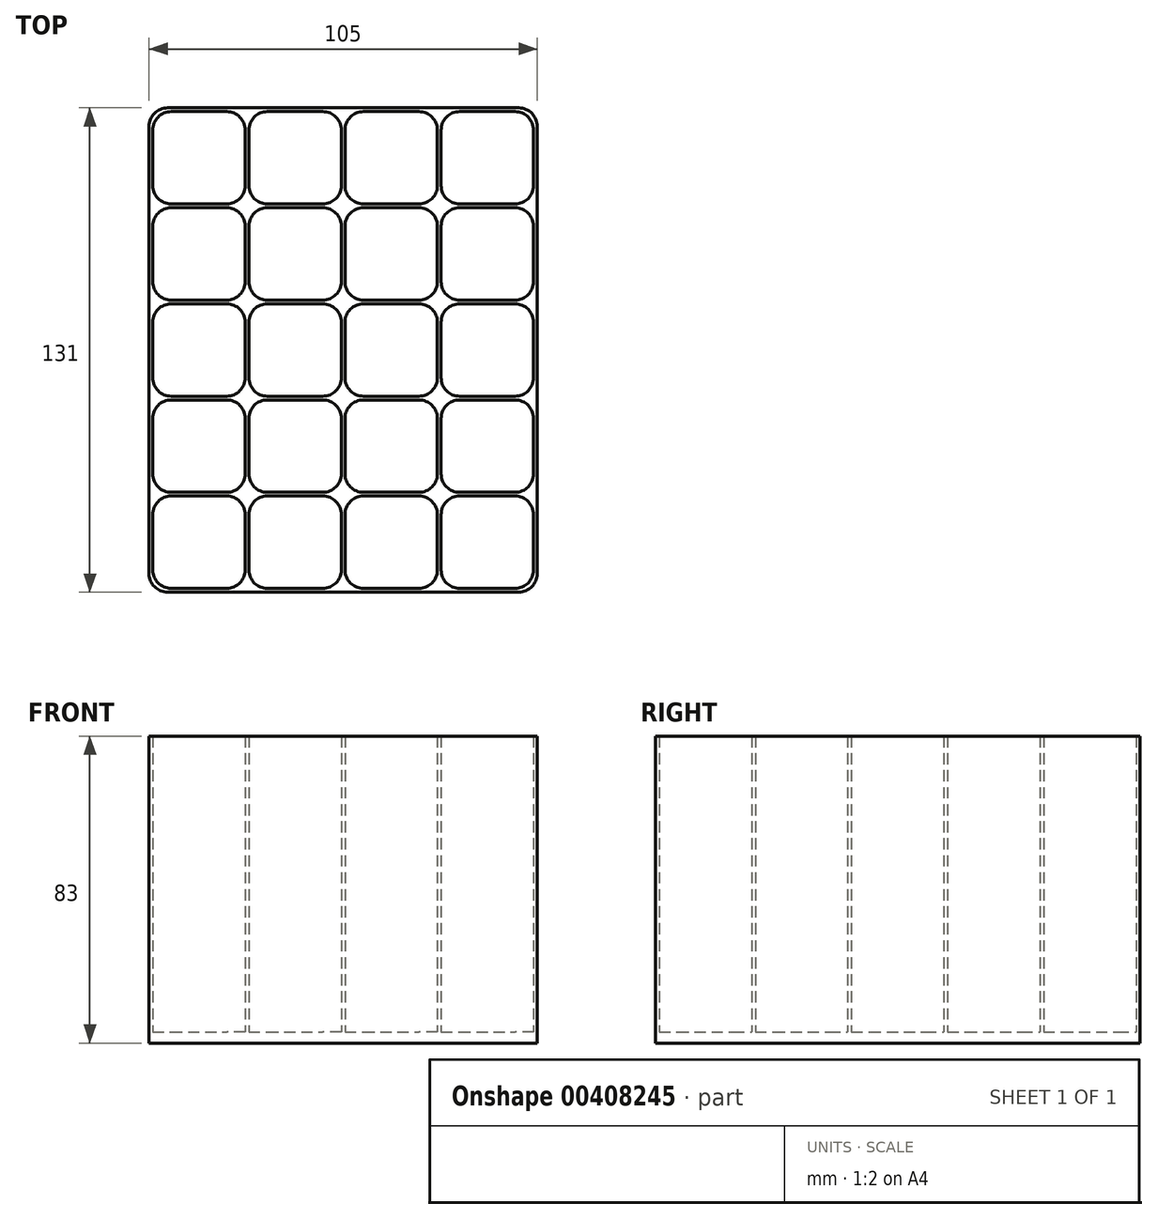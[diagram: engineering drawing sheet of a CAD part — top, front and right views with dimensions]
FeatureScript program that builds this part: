
annotation { "Feature Type Name" : "Feature", "Feature Type Description" : "" }
export const myFeature = defineFeature(function(context is Context, id is Id, definition is map)
    precondition{}
    {
        {
            var Q0;
            Q0=qCreatedBy(makeId("Top.planeOp"),FACE);
            var sketch = newSketch(context, id + "F0", { "sketchPlane" : qUnion([Q0])});
            skLineSegment(sketch, "E0.bottom", {"start": v(5, 0) * mm, "end": v(20, 0) * mm});
            skLineSegment(sketch, "E0.top", {"start": v(5, 25) * mm, "end": v(20, 25) * mm});
            skLineSegment(sketch, "E0.left", {"start": v(0, 5) * mm, "end": v(0, 20) * mm});
            skLineSegment(sketch, "E0.right", {"start": v(25, 5) * mm, "end": v(25, 20) * mm});
            skPoint(sketch, "E1.visualSharp", {"position": v(0, 25) * mm});
            skArc(sketch, "E1.filletArc", {"start": v(5, 25) * mm, "mid": v(1.46, 23.54) * mm, "end": v(0, 20) * mm});
            skPoint(sketch, "E2.visualSharp", {"position": v(25, 25) * mm});
            skArc(sketch, "E2.filletArc", {"start": v(25, 20) * mm, "mid": v(23.54, 23.54) * mm, "end": v(20, 25) * mm});
            skPoint(sketch, "E3.visualSharp", {"position": v(25, 0) * mm});
            skArc(sketch, "E3.filletArc", {"start": v(20, 0) * mm, "mid": v(23.54, 1.46) * mm, "end": v(25, 5) * mm});
            skPoint(sketch, "E4.visualSharp", {"position": v(0, 0) * mm});
            skArc(sketch, "E4.filletArc", {"start": v(0, 5) * mm, "mid": v(1.46, 1.46) * mm, "end": v(5, 0) * mm});
            skPoint(sketch, "E5.0.1.0", {"position": v(25, 51) * mm});
            skLineSegment(sketch, "E5.0.1.1", {"start": v(25, 31) * mm, "end": v(25, 46) * mm});
            skLineSegment(sketch, "E5.0.1.2", {"start": v(0, 31) * mm, "end": v(0, 46) * mm});
            skPoint(sketch, "E5.0.1.3", {"position": v(25, 26) * mm});
            skPoint(sketch, "E5.0.1.4", {"position": v(0, 51) * mm});
            skLineSegment(sketch, "E5.0.1.5", {"start": v(5, 51) * mm, "end": v(20, 51) * mm});
            skLineSegment(sketch, "E5.0.1.6", {"start": v(5, 26) * mm, "end": v(20, 26) * mm});
            skPoint(sketch, "E5.0.1.7", {"position": v(0, 26) * mm});
            skArc(sketch, "E5.0.1.8", {"start": v(25, 46) * mm, "mid": v(23.54, 49.54) * mm, "end": v(20, 51) * mm});
            skArc(sketch, "E5.0.1.9", {"start": v(5, 51) * mm, "mid": v(1.46, 49.54) * mm, "end": v(0, 46) * mm});
            skArc(sketch, "E5.0.1.10", {"start": v(20, 26) * mm, "mid": v(23.54, 27.46) * mm, "end": v(25, 31) * mm});
            skArc(sketch, "E5.0.1.11", {"start": v(0, 31) * mm, "mid": v(1.46, 27.46) * mm, "end": v(5, 26) * mm});
            skPoint(sketch, "E5.0.2.0", {"position": v(25, 77) * mm});
            skLineSegment(sketch, "E5.0.2.1", {"start": v(25, 57) * mm, "end": v(25, 72) * mm});
            skLineSegment(sketch, "E5.0.2.2", {"start": v(0, 57) * mm, "end": v(0, 72) * mm});
            skPoint(sketch, "E5.0.2.3", {"position": v(25, 52) * mm});
            skPoint(sketch, "E5.0.2.4", {"position": v(0, 77) * mm});
            skLineSegment(sketch, "E5.0.2.5", {"start": v(5, 77) * mm, "end": v(20, 77) * mm});
            skLineSegment(sketch, "E5.0.2.6", {"start": v(5, 52) * mm, "end": v(20, 52) * mm});
            skPoint(sketch, "E5.0.2.7", {"position": v(0, 52) * mm});
            skArc(sketch, "E5.0.2.8", {"start": v(25, 72) * mm, "mid": v(23.54, 75.54) * mm, "end": v(20, 77) * mm});
            skArc(sketch, "E5.0.2.9", {"start": v(5, 77) * mm, "mid": v(1.46, 75.54) * mm, "end": v(0, 72) * mm});
            skArc(sketch, "E5.0.2.10", {"start": v(20, 52) * mm, "mid": v(23.54, 53.46) * mm, "end": v(25, 57) * mm});
            skArc(sketch, "E5.0.2.11", {"start": v(0, 57) * mm, "mid": v(1.46, 53.46) * mm, "end": v(5, 52) * mm});
            skPoint(sketch, "E5.0.3.0", {"position": v(25, 103) * mm});
            skLineSegment(sketch, "E5.0.3.1", {"start": v(25, 83) * mm, "end": v(25, 98) * mm});
            skLineSegment(sketch, "E5.0.3.2", {"start": v(0, 83) * mm, "end": v(0, 98) * mm});
            skPoint(sketch, "E5.0.3.3", {"position": v(25, 78) * mm});
            skPoint(sketch, "E5.0.3.4", {"position": v(0, 103) * mm});
            skLineSegment(sketch, "E5.0.3.5", {"start": v(5, 103) * mm, "end": v(20, 103) * mm});
            skLineSegment(sketch, "E5.0.3.6", {"start": v(5, 78) * mm, "end": v(20, 78) * mm});
            skPoint(sketch, "E5.0.3.7", {"position": v(0, 78) * mm});
            skArc(sketch, "E5.0.3.8", {"start": v(25, 98) * mm, "mid": v(23.54, 101.54) * mm, "end": v(20, 103) * mm});
            skArc(sketch, "E5.0.3.9", {"start": v(5, 103) * mm, "mid": v(1.46, 101.54) * mm, "end": v(0, 98) * mm});
            skArc(sketch, "E5.0.3.10", {"start": v(20, 78) * mm, "mid": v(23.54, 79.46) * mm, "end": v(25, 83) * mm});
            skArc(sketch, "E5.0.3.11", {"start": v(0, 83) * mm, "mid": v(1.46, 79.46) * mm, "end": v(5, 78) * mm});
            skPoint(sketch, "E5.0.4.0", {"position": v(25, 129) * mm});
            skLineSegment(sketch, "E5.0.4.1", {"start": v(25, 109) * mm, "end": v(25, 124) * mm});
            skLineSegment(sketch, "E5.0.4.2", {"start": v(0, 109) * mm, "end": v(0, 124) * mm});
            skPoint(sketch, "E5.0.4.3", {"position": v(25, 104) * mm});
            skPoint(sketch, "E5.0.4.4", {"position": v(0, 129) * mm});
            skLineSegment(sketch, "E5.0.4.5", {"start": v(5, 129) * mm, "end": v(20, 129) * mm});
            skLineSegment(sketch, "E5.0.4.6", {"start": v(5, 104) * mm, "end": v(20, 104) * mm});
            skPoint(sketch, "E5.0.4.7", {"position": v(0, 104) * mm});
            skArc(sketch, "E5.0.4.8", {"start": v(25, 124) * mm, "mid": v(23.54, 127.54) * mm, "end": v(20, 129) * mm});
            skArc(sketch, "E5.0.4.9", {"start": v(5, 129) * mm, "mid": v(1.46, 127.54) * mm, "end": v(0, 124) * mm});
            skArc(sketch, "E5.0.4.10", {"start": v(20, 104) * mm, "mid": v(23.54, 105.46) * mm, "end": v(25, 109) * mm});
            skArc(sketch, "E5.0.4.11", {"start": v(0, 109) * mm, "mid": v(1.46, 105.46) * mm, "end": v(5, 104) * mm});
            skPoint(sketch, "E5.1.0.0", {"position": v(51, 25) * mm});
            skLineSegment(sketch, "E5.1.0.1", {"start": v(51, 5) * mm, "end": v(51, 20) * mm});
            skLineSegment(sketch, "E5.1.0.2", {"start": v(26, 5) * mm, "end": v(26, 20) * mm});
            skPoint(sketch, "E5.1.0.3", {"position": v(51, 0) * mm});
            skPoint(sketch, "E5.1.0.4", {"position": v(26, 25) * mm});
            skLineSegment(sketch, "E5.1.0.5", {"start": v(31, 25) * mm, "end": v(46, 25) * mm});
            skLineSegment(sketch, "E5.1.0.6", {"start": v(31, 0) * mm, "end": v(46, 0) * mm});
            skPoint(sketch, "E5.1.0.7", {"position": v(26, 0) * mm});
            skArc(sketch, "E5.1.0.8", {"start": v(51, 20) * mm, "mid": v(49.54, 23.54) * mm, "end": v(46, 25) * mm});
            skArc(sketch, "E5.1.0.9", {"start": v(31, 25) * mm, "mid": v(27.46, 23.54) * mm, "end": v(26, 20) * mm});
            skArc(sketch, "E5.1.0.10", {"start": v(46, 0) * mm, "mid": v(49.54, 1.46) * mm, "end": v(51, 5) * mm});
            skArc(sketch, "E5.1.0.11", {"start": v(26, 5) * mm, "mid": v(27.46, 1.46) * mm, "end": v(31, 0) * mm});
            skPoint(sketch, "E5.1.1.0", {"position": v(51, 51) * mm});
            skLineSegment(sketch, "E5.1.1.1", {"start": v(51, 31) * mm, "end": v(51, 46) * mm});
            skLineSegment(sketch, "E5.1.1.2", {"start": v(26, 31) * mm, "end": v(26, 46) * mm});
            skPoint(sketch, "E5.1.1.3", {"position": v(51, 26) * mm});
            skPoint(sketch, "E5.1.1.4", {"position": v(26, 51) * mm});
            skLineSegment(sketch, "E5.1.1.5", {"start": v(31, 51) * mm, "end": v(46, 51) * mm});
            skLineSegment(sketch, "E5.1.1.6", {"start": v(31, 26) * mm, "end": v(46, 26) * mm});
            skPoint(sketch, "E5.1.1.7", {"position": v(26, 26) * mm});
            skArc(sketch, "E5.1.1.8", {"start": v(51, 46) * mm, "mid": v(49.54, 49.54) * mm, "end": v(46, 51) * mm});
            skArc(sketch, "E5.1.1.9", {"start": v(31, 51) * mm, "mid": v(27.46, 49.54) * mm, "end": v(26, 46) * mm});
            skArc(sketch, "E5.1.1.10", {"start": v(46, 26) * mm, "mid": v(49.54, 27.46) * mm, "end": v(51, 31) * mm});
            skArc(sketch, "E5.1.1.11", {"start": v(26, 31) * mm, "mid": v(27.46, 27.46) * mm, "end": v(31, 26) * mm});
            skPoint(sketch, "E5.1.2.0", {"position": v(51, 77) * mm});
            skLineSegment(sketch, "E5.1.2.1", {"start": v(51, 57) * mm, "end": v(51, 72) * mm});
            skLineSegment(sketch, "E5.1.2.2", {"start": v(26, 57) * mm, "end": v(26, 72) * mm});
            skPoint(sketch, "E5.1.2.3", {"position": v(51, 52) * mm});
            skPoint(sketch, "E5.1.2.4", {"position": v(26, 77) * mm});
            skLineSegment(sketch, "E5.1.2.5", {"start": v(31, 77) * mm, "end": v(46, 77) * mm});
            skLineSegment(sketch, "E5.1.2.6", {"start": v(31, 52) * mm, "end": v(46, 52) * mm});
            skPoint(sketch, "E5.1.2.7", {"position": v(26, 52) * mm});
            skArc(sketch, "E5.1.2.8", {"start": v(51, 72) * mm, "mid": v(49.54, 75.54) * mm, "end": v(46, 77) * mm});
            skArc(sketch, "E5.1.2.9", {"start": v(31, 77) * mm, "mid": v(27.46, 75.54) * mm, "end": v(26, 72) * mm});
            skArc(sketch, "E5.1.2.10", {"start": v(46, 52) * mm, "mid": v(49.54, 53.46) * mm, "end": v(51, 57) * mm});
            skArc(sketch, "E5.1.2.11", {"start": v(26, 57) * mm, "mid": v(27.46, 53.46) * mm, "end": v(31, 52) * mm});
            skPoint(sketch, "E5.1.3.0", {"position": v(51, 103) * mm});
            skLineSegment(sketch, "E5.1.3.1", {"start": v(51, 83) * mm, "end": v(51, 98) * mm});
            skLineSegment(sketch, "E5.1.3.2", {"start": v(26, 83) * mm, "end": v(26, 98) * mm});
            skPoint(sketch, "E5.1.3.3", {"position": v(51, 78) * mm});
            skPoint(sketch, "E5.1.3.4", {"position": v(26, 103) * mm});
            skLineSegment(sketch, "E5.1.3.5", {"start": v(31, 103) * mm, "end": v(46, 103) * mm});
            skLineSegment(sketch, "E5.1.3.6", {"start": v(31, 78) * mm, "end": v(46, 78) * mm});
            skPoint(sketch, "E5.1.3.7", {"position": v(26, 78) * mm});
            skArc(sketch, "E5.1.3.8", {"start": v(51, 98) * mm, "mid": v(49.54, 101.54) * mm, "end": v(46, 103) * mm});
            skArc(sketch, "E5.1.3.9", {"start": v(31, 103) * mm, "mid": v(27.46, 101.54) * mm, "end": v(26, 98) * mm});
            skArc(sketch, "E5.1.3.10", {"start": v(46, 78) * mm, "mid": v(49.54, 79.46) * mm, "end": v(51, 83) * mm});
            skArc(sketch, "E5.1.3.11", {"start": v(26, 83) * mm, "mid": v(27.46, 79.46) * mm, "end": v(31, 78) * mm});
            skPoint(sketch, "E5.1.4.0", {"position": v(51, 129) * mm});
            skLineSegment(sketch, "E5.1.4.1", {"start": v(51, 109) * mm, "end": v(51, 124) * mm});
            skLineSegment(sketch, "E5.1.4.2", {"start": v(26, 109) * mm, "end": v(26, 124) * mm});
            skPoint(sketch, "E5.1.4.3", {"position": v(51, 104) * mm});
            skPoint(sketch, "E5.1.4.4", {"position": v(26, 129) * mm});
            skLineSegment(sketch, "E5.1.4.5", {"start": v(31, 129) * mm, "end": v(46, 129) * mm});
            skLineSegment(sketch, "E5.1.4.6", {"start": v(31, 104) * mm, "end": v(46, 104) * mm});
            skPoint(sketch, "E5.1.4.7", {"position": v(26, 104) * mm});
            skArc(sketch, "E5.1.4.8", {"start": v(51, 124) * mm, "mid": v(49.54, 127.54) * mm, "end": v(46, 129) * mm});
            skArc(sketch, "E5.1.4.9", {"start": v(31, 129) * mm, "mid": v(27.46, 127.54) * mm, "end": v(26, 124) * mm});
            skArc(sketch, "E5.1.4.10", {"start": v(46, 104) * mm, "mid": v(49.54, 105.46) * mm, "end": v(51, 109) * mm});
            skArc(sketch, "E5.1.4.11", {"start": v(26, 109) * mm, "mid": v(27.46, 105.46) * mm, "end": v(31, 104) * mm});
            skPoint(sketch, "E5.2.0.0", {"position": v(77, 25) * mm});
            skLineSegment(sketch, "E5.2.0.1", {"start": v(77, 5) * mm, "end": v(77, 20) * mm});
            skLineSegment(sketch, "E5.2.0.2", {"start": v(52, 5) * mm, "end": v(52, 20) * mm});
            skPoint(sketch, "E5.2.0.3", {"position": v(77, 0) * mm});
            skPoint(sketch, "E5.2.0.4", {"position": v(52, 25) * mm});
            skLineSegment(sketch, "E5.2.0.5", {"start": v(57, 25) * mm, "end": v(72, 25) * mm});
            skLineSegment(sketch, "E5.2.0.6", {"start": v(57, 0) * mm, "end": v(72, 0) * mm});
            skPoint(sketch, "E5.2.0.7", {"position": v(52, 0) * mm});
            skArc(sketch, "E5.2.0.8", {"start": v(77, 20) * mm, "mid": v(75.54, 23.54) * mm, "end": v(72, 25) * mm});
            skArc(sketch, "E5.2.0.9", {"start": v(57, 25) * mm, "mid": v(53.46, 23.54) * mm, "end": v(52, 20) * mm});
            skArc(sketch, "E5.2.0.10", {"start": v(72, 0) * mm, "mid": v(75.54, 1.46) * mm, "end": v(77, 5) * mm});
            skArc(sketch, "E5.2.0.11", {"start": v(52, 5) * mm, "mid": v(53.46, 1.46) * mm, "end": v(57, 0) * mm});
            skPoint(sketch, "E5.2.1.0", {"position": v(77, 51) * mm});
            skLineSegment(sketch, "E5.2.1.1", {"start": v(77, 31) * mm, "end": v(77, 46) * mm});
            skLineSegment(sketch, "E5.2.1.2", {"start": v(52, 31) * mm, "end": v(52, 46) * mm});
            skPoint(sketch, "E5.2.1.3", {"position": v(77, 26) * mm});
            skPoint(sketch, "E5.2.1.4", {"position": v(52, 51) * mm});
            skLineSegment(sketch, "E5.2.1.5", {"start": v(57, 51) * mm, "end": v(72, 51) * mm});
            skLineSegment(sketch, "E5.2.1.6", {"start": v(57, 26) * mm, "end": v(72, 26) * mm});
            skPoint(sketch, "E5.2.1.7", {"position": v(52, 26) * mm});
            skArc(sketch, "E5.2.1.8", {"start": v(77, 46) * mm, "mid": v(75.54, 49.54) * mm, "end": v(72, 51) * mm});
            skArc(sketch, "E5.2.1.9", {"start": v(57, 51) * mm, "mid": v(53.46, 49.54) * mm, "end": v(52, 46) * mm});
            skArc(sketch, "E5.2.1.10", {"start": v(72, 26) * mm, "mid": v(75.54, 27.46) * mm, "end": v(77, 31) * mm});
            skArc(sketch, "E5.2.1.11", {"start": v(52, 31) * mm, "mid": v(53.46, 27.46) * mm, "end": v(57, 26) * mm});
            skPoint(sketch, "E5.2.2.0", {"position": v(77, 77) * mm});
            skLineSegment(sketch, "E5.2.2.1", {"start": v(77, 57) * mm, "end": v(77, 72) * mm});
            skLineSegment(sketch, "E5.2.2.2", {"start": v(52, 57) * mm, "end": v(52, 72) * mm});
            skPoint(sketch, "E5.2.2.3", {"position": v(77, 52) * mm});
            skPoint(sketch, "E5.2.2.4", {"position": v(52, 77) * mm});
            skLineSegment(sketch, "E5.2.2.5", {"start": v(57, 77) * mm, "end": v(72, 77) * mm});
            skLineSegment(sketch, "E5.2.2.6", {"start": v(57, 52) * mm, "end": v(72, 52) * mm});
            skPoint(sketch, "E5.2.2.7", {"position": v(52, 52) * mm});
            skArc(sketch, "E5.2.2.8", {"start": v(77, 72) * mm, "mid": v(75.54, 75.54) * mm, "end": v(72, 77) * mm});
            skArc(sketch, "E5.2.2.9", {"start": v(57, 77) * mm, "mid": v(53.46, 75.54) * mm, "end": v(52, 72) * mm});
            skArc(sketch, "E5.2.2.10", {"start": v(72, 52) * mm, "mid": v(75.54, 53.46) * mm, "end": v(77, 57) * mm});
            skArc(sketch, "E5.2.2.11", {"start": v(52, 57) * mm, "mid": v(53.46, 53.46) * mm, "end": v(57, 52) * mm});
            skPoint(sketch, "E5.2.3.0", {"position": v(77, 103) * mm});
            skLineSegment(sketch, "E5.2.3.1", {"start": v(77, 83) * mm, "end": v(77, 98) * mm});
            skLineSegment(sketch, "E5.2.3.2", {"start": v(52, 83) * mm, "end": v(52, 98) * mm});
            skPoint(sketch, "E5.2.3.3", {"position": v(77, 78) * mm});
            skPoint(sketch, "E5.2.3.4", {"position": v(52, 103) * mm});
            skLineSegment(sketch, "E5.2.3.5", {"start": v(57, 103) * mm, "end": v(72, 103) * mm});
            skLineSegment(sketch, "E5.2.3.6", {"start": v(57, 78) * mm, "end": v(72, 78) * mm});
            skPoint(sketch, "E5.2.3.7", {"position": v(52, 78) * mm});
            skArc(sketch, "E5.2.3.8", {"start": v(77, 98) * mm, "mid": v(75.54, 101.54) * mm, "end": v(72, 103) * mm});
            skArc(sketch, "E5.2.3.9", {"start": v(57, 103) * mm, "mid": v(53.46, 101.54) * mm, "end": v(52, 98) * mm});
            skArc(sketch, "E5.2.3.10", {"start": v(72, 78) * mm, "mid": v(75.54, 79.46) * mm, "end": v(77, 83) * mm});
            skArc(sketch, "E5.2.3.11", {"start": v(52, 83) * mm, "mid": v(53.46, 79.46) * mm, "end": v(57, 78) * mm});
            skPoint(sketch, "E5.2.4.0", {"position": v(77, 129) * mm});
            skLineSegment(sketch, "E5.2.4.1", {"start": v(77, 109) * mm, "end": v(77, 124) * mm});
            skLineSegment(sketch, "E5.2.4.2", {"start": v(52, 109) * mm, "end": v(52, 124) * mm});
            skPoint(sketch, "E5.2.4.3", {"position": v(77, 104) * mm});
            skPoint(sketch, "E5.2.4.4", {"position": v(52, 129) * mm});
            skLineSegment(sketch, "E5.2.4.5", {"start": v(57, 129) * mm, "end": v(72, 129) * mm});
            skLineSegment(sketch, "E5.2.4.6", {"start": v(57, 104) * mm, "end": v(72, 104) * mm});
            skPoint(sketch, "E5.2.4.7", {"position": v(52, 104) * mm});
            skArc(sketch, "E5.2.4.8", {"start": v(77, 124) * mm, "mid": v(75.54, 127.54) * mm, "end": v(72, 129) * mm});
            skArc(sketch, "E5.2.4.9", {"start": v(57, 129) * mm, "mid": v(53.46, 127.54) * mm, "end": v(52, 124) * mm});
            skArc(sketch, "E5.2.4.10", {"start": v(72, 104) * mm, "mid": v(75.54, 105.46) * mm, "end": v(77, 109) * mm});
            skArc(sketch, "E5.2.4.11", {"start": v(52, 109) * mm, "mid": v(53.46, 105.46) * mm, "end": v(57, 104) * mm});
            skPoint(sketch, "E5.3.0.0", {"position": v(103, 25) * mm});
            skLineSegment(sketch, "E5.3.0.1", {"start": v(103, 5) * mm, "end": v(103, 20) * mm});
            skLineSegment(sketch, "E5.3.0.2", {"start": v(78, 5) * mm, "end": v(78, 20) * mm});
            skPoint(sketch, "E5.3.0.3", {"position": v(103, 0) * mm});
            skPoint(sketch, "E5.3.0.4", {"position": v(78, 25) * mm});
            skLineSegment(sketch, "E5.3.0.5", {"start": v(83, 25) * mm, "end": v(98, 25) * mm});
            skLineSegment(sketch, "E5.3.0.6", {"start": v(83, 0) * mm, "end": v(98, 0) * mm});
            skPoint(sketch, "E5.3.0.7", {"position": v(78, 0) * mm});
            skArc(sketch, "E5.3.0.8", {"start": v(103, 20) * mm, "mid": v(101.54, 23.54) * mm, "end": v(98, 25) * mm});
            skArc(sketch, "E5.3.0.9", {"start": v(83, 25) * mm, "mid": v(79.46, 23.54) * mm, "end": v(78, 20) * mm});
            skArc(sketch, "E5.3.0.10", {"start": v(98, 0) * mm, "mid": v(101.54, 1.46) * mm, "end": v(103, 5) * mm});
            skArc(sketch, "E5.3.0.11", {"start": v(78, 5) * mm, "mid": v(79.46, 1.46) * mm, "end": v(83, 0) * mm});
            skPoint(sketch, "E5.3.1.0", {"position": v(103, 51) * mm});
            skLineSegment(sketch, "E5.3.1.1", {"start": v(103, 31) * mm, "end": v(103, 46) * mm});
            skLineSegment(sketch, "E5.3.1.2", {"start": v(78, 31) * mm, "end": v(78, 46) * mm});
            skPoint(sketch, "E5.3.1.3", {"position": v(103, 26) * mm});
            skPoint(sketch, "E5.3.1.4", {"position": v(78, 51) * mm});
            skLineSegment(sketch, "E5.3.1.5", {"start": v(83, 51) * mm, "end": v(98, 51) * mm});
            skLineSegment(sketch, "E5.3.1.6", {"start": v(83, 26) * mm, "end": v(98, 26) * mm});
            skPoint(sketch, "E5.3.1.7", {"position": v(78, 26) * mm});
            skArc(sketch, "E5.3.1.8", {"start": v(103, 46) * mm, "mid": v(101.54, 49.54) * mm, "end": v(98, 51) * mm});
            skArc(sketch, "E5.3.1.9", {"start": v(83, 51) * mm, "mid": v(79.46, 49.54) * mm, "end": v(78, 46) * mm});
            skArc(sketch, "E5.3.1.10", {"start": v(98, 26) * mm, "mid": v(101.54, 27.46) * mm, "end": v(103, 31) * mm});
            skArc(sketch, "E5.3.1.11", {"start": v(78, 31) * mm, "mid": v(79.46, 27.46) * mm, "end": v(83, 26) * mm});
            skPoint(sketch, "E5.3.2.0", {"position": v(103, 77) * mm});
            skLineSegment(sketch, "E5.3.2.1", {"start": v(103, 57) * mm, "end": v(103, 72) * mm});
            skLineSegment(sketch, "E5.3.2.2", {"start": v(78, 57) * mm, "end": v(78, 72) * mm});
            skPoint(sketch, "E5.3.2.3", {"position": v(103, 52) * mm});
            skPoint(sketch, "E5.3.2.4", {"position": v(78, 77) * mm});
            skLineSegment(sketch, "E5.3.2.5", {"start": v(83, 77) * mm, "end": v(98, 77) * mm});
            skLineSegment(sketch, "E5.3.2.6", {"start": v(83, 52) * mm, "end": v(98, 52) * mm});
            skPoint(sketch, "E5.3.2.7", {"position": v(78, 52) * mm});
            skArc(sketch, "E5.3.2.8", {"start": v(103, 72) * mm, "mid": v(101.54, 75.54) * mm, "end": v(98, 77) * mm});
            skArc(sketch, "E5.3.2.9", {"start": v(83, 77) * mm, "mid": v(79.46, 75.54) * mm, "end": v(78, 72) * mm});
            skArc(sketch, "E5.3.2.10", {"start": v(98, 52) * mm, "mid": v(101.54, 53.46) * mm, "end": v(103, 57) * mm});
            skArc(sketch, "E5.3.2.11", {"start": v(78, 57) * mm, "mid": v(79.46, 53.46) * mm, "end": v(83, 52) * mm});
            skPoint(sketch, "E5.3.3.0", {"position": v(103, 103) * mm});
            skLineSegment(sketch, "E5.3.3.1", {"start": v(103, 83) * mm, "end": v(103, 98) * mm});
            skLineSegment(sketch, "E5.3.3.2", {"start": v(78, 83) * mm, "end": v(78, 98) * mm});
            skPoint(sketch, "E5.3.3.3", {"position": v(103, 78) * mm});
            skPoint(sketch, "E5.3.3.4", {"position": v(78, 103) * mm});
            skLineSegment(sketch, "E5.3.3.5", {"start": v(83, 103) * mm, "end": v(98, 103) * mm});
            skLineSegment(sketch, "E5.3.3.6", {"start": v(83, 78) * mm, "end": v(98, 78) * mm});
            skPoint(sketch, "E5.3.3.7", {"position": v(78, 78) * mm});
            skArc(sketch, "E5.3.3.8", {"start": v(103, 98) * mm, "mid": v(101.54, 101.54) * mm, "end": v(98, 103) * mm});
            skArc(sketch, "E5.3.3.9", {"start": v(83, 103) * mm, "mid": v(79.46, 101.54) * mm, "end": v(78, 98) * mm});
            skArc(sketch, "E5.3.3.10", {"start": v(98, 78) * mm, "mid": v(101.54, 79.46) * mm, "end": v(103, 83) * mm});
            skArc(sketch, "E5.3.3.11", {"start": v(78, 83) * mm, "mid": v(79.46, 79.46) * mm, "end": v(83, 78) * mm});
            skPoint(sketch, "E5.3.4.0", {"position": v(103, 129) * mm});
            skLineSegment(sketch, "E5.3.4.1", {"start": v(103, 109) * mm, "end": v(103, 124) * mm});
            skLineSegment(sketch, "E5.3.4.2", {"start": v(78, 109) * mm, "end": v(78, 124) * mm});
            skPoint(sketch, "E5.3.4.3", {"position": v(103, 104) * mm});
            skPoint(sketch, "E5.3.4.4", {"position": v(78, 129) * mm});
            skLineSegment(sketch, "E5.3.4.5", {"start": v(83, 129) * mm, "end": v(98, 129) * mm});
            skLineSegment(sketch, "E5.3.4.6", {"start": v(83, 104) * mm, "end": v(98, 104) * mm});
            skPoint(sketch, "E5.3.4.7", {"position": v(78, 104) * mm});
            skArc(sketch, "E5.3.4.8", {"start": v(103, 124) * mm, "mid": v(101.54, 127.54) * mm, "end": v(98, 129) * mm});
            skArc(sketch, "E5.3.4.9", {"start": v(83, 129) * mm, "mid": v(79.46, 127.54) * mm, "end": v(78, 124) * mm});
            skArc(sketch, "E5.3.4.10", {"start": v(98, 104) * mm, "mid": v(101.54, 105.46) * mm, "end": v(103, 109) * mm});
            skArc(sketch, "E5.3.4.11", {"start": v(78, 109) * mm, "mid": v(79.46, 105.46) * mm, "end": v(83, 104) * mm});
            skLineSegment(sketch, "E5.direction1", {"start": v(0, 0) * mm, "end": v(26, 0) * mm, "construction": true});
            skLineSegment(sketch, "E5.direction2", {"start": v(0, 0) * mm, "end": v(0, 26) * mm, "construction": true});
            skLineSegment(sketch, "E6.bottom", {"start": v(4, -1) * mm, "end": v(99, -1) * mm});
            skLineSegment(sketch, "E6.top", {"start": v(4, 130) * mm, "end": v(99, 130) * mm});
            skLineSegment(sketch, "E6.left", {"start": v(-1, 4) * mm, "end": v(-1, 125) * mm});
            skLineSegment(sketch, "E6.right", {"start": v(104, 4) * mm, "end": v(104, 125) * mm});
            skPoint(sketch, "E7.visualSharp", {"position": v(-1, 130) * mm});
            skArc(sketch, "E7.filletArc", {"start": v(4, 130) * mm, "mid": v(0.46, 128.54) * mm, "end": v(-1, 125) * mm});
            skPoint(sketch, "E8.visualSharp", {"position": v(104, 130) * mm});
            skArc(sketch, "E8.filletArc", {"start": v(104, 125) * mm, "mid": v(102.54, 128.54) * mm, "end": v(99, 130) * mm});
            skPoint(sketch, "E9.visualSharp", {"position": v(104, -1) * mm});
            skArc(sketch, "E9.filletArc", {"start": v(99, -1) * mm, "mid": v(102.54, 0.46) * mm, "end": v(104, 4) * mm});
            skPoint(sketch, "E10.visualSharp", {"position": v(-1, -1) * mm});
            skArc(sketch, "E10.filletArc", {"start": v(-1, 4) * mm, "mid": v(0.46, 0.46) * mm, "end": v(4, -1) * mm});
            skSolve(sketch);
        }
        {
            var Q0;
            Q0=makeQuery(id+"F0.imprint","IMPRINT",FACE,{"disambiguationData":[TD([[makeQuery(id+"F0.imprint","IMPRINT",EDGE,{"derivedFrom":sQuery(id+"F0.wireOp",EDGE,"E0.bottom")}),-1.0]])]});
            extrude(context, id + "F1", {"entities" : qUnion([Q0]), "depth" : 80 * mm});
        }
        {
            var Q0;
            Q0=makeQuery(id+"F0.imprint","IMPRINT",FACE,{"disambiguationData":[TD([[makeQuery(id+"F0.imprint","IMPRINT",EDGE,{"derivedFrom":sQuery(id+"F0.wireOp",EDGE,"E5.3.0.1")}),1.0]])]});
            var Q1;
            Q1=makeQuery(id+"F0.imprint","IMPRINT",FACE,{"disambiguationData":[TD([[makeQuery(id+"F0.imprint","IMPRINT",EDGE,{"derivedFrom":sQuery(id+"F0.wireOp",EDGE,"E5.0.4.1")}),1.0]])]});
            var Q2;
            Q2=makeQuery(id+"F0.imprint","IMPRINT",FACE,{"disambiguationData":[TD([[makeQuery(id+"F0.imprint","IMPRINT",EDGE,{"derivedFrom":sQuery(id+"F0.wireOp",EDGE,"E5.0.3.1")}),1.0]])]});
            var Q3;
            Q3=makeQuery(id+"F0.imprint","IMPRINT",FACE,{"disambiguationData":[TD([[makeQuery(id+"F0.imprint","IMPRINT",EDGE,{"derivedFrom":sQuery(id+"F0.wireOp",EDGE,"E5.0.2.1")}),1.0]])]});
            var Q4;
            Q4=makeQuery(id+"F0.imprint","IMPRINT",FACE,{"disambiguationData":[TD([[makeQuery(id+"F0.imprint","IMPRINT",EDGE,{"derivedFrom":sQuery(id+"F0.wireOp",EDGE,"E5.0.1.1")}),1.0]])]});
            var Q5;
            Q5=makeQuery(id+"F0.imprint","IMPRINT",FACE,{"disambiguationData":[TD([[makeQuery(id+"F0.imprint","IMPRINT",EDGE,{"derivedFrom":sQuery(id+"F0.wireOp",EDGE,"E5.1.0.1")}),1.0]])]});
            var Q6;
            Q6=makeQuery(id+"F0.imprint","IMPRINT",FACE,{"disambiguationData":[TD([[makeQuery(id+"F0.imprint","IMPRINT",EDGE,{"derivedFrom":sQuery(id+"F0.wireOp",EDGE,"E5.1.1.1")}),1.0]])]});
            var Q7;
            Q7=makeQuery(id+"F0.imprint","IMPRINT",FACE,{"disambiguationData":[TD([[makeQuery(id+"F0.imprint","IMPRINT",EDGE,{"derivedFrom":sQuery(id+"F0.wireOp",EDGE,"E5.1.2.1")}),1.0]])]});
            var Q8;
            Q8=makeQuery(id+"F0.imprint","IMPRINT",FACE,{"disambiguationData":[TD([[makeQuery(id+"F0.imprint","IMPRINT",EDGE,{"derivedFrom":sQuery(id+"F0.wireOp",EDGE,"E5.1.3.1")}),1.0]])]});
            var Q9;
            Q9=makeQuery(id+"F0.imprint","IMPRINT",FACE,{"disambiguationData":[TD([[makeQuery(id+"F0.imprint","IMPRINT",EDGE,{"derivedFrom":sQuery(id+"F0.wireOp",EDGE,"E5.1.4.1")}),1.0]])]});
            var Q10;
            Q10=makeQuery(id+"F0.imprint","IMPRINT",FACE,{"disambiguationData":[TD([[makeQuery(id+"F0.imprint","IMPRINT",EDGE,{"derivedFrom":sQuery(id+"F0.wireOp",EDGE,"E5.2.4.1")}),1.0]])]});
            var Q11;
            Q11=makeQuery(id+"F0.imprint","IMPRINT",FACE,{"disambiguationData":[TD([[makeQuery(id+"F0.imprint","IMPRINT",EDGE,{"derivedFrom":sQuery(id+"F0.wireOp",EDGE,"E5.2.3.1")}),1.0]])]});
            var Q12;
            Q12=makeQuery(id+"F0.imprint","IMPRINT",FACE,{"disambiguationData":[TD([[makeQuery(id+"F0.imprint","IMPRINT",EDGE,{"derivedFrom":sQuery(id+"F0.wireOp",EDGE,"E5.2.2.1")}),1.0]])]});
            var Q13;
            Q13=makeQuery(id+"F0.imprint","IMPRINT",FACE,{"disambiguationData":[TD([[makeQuery(id+"F0.imprint","IMPRINT",EDGE,{"derivedFrom":sQuery(id+"F0.wireOp",EDGE,"E5.2.1.1")}),1.0]])]});
            var Q14;
            Q14=makeQuery(id+"F0.imprint","IMPRINT",FACE,{"disambiguationData":[TD([[makeQuery(id+"F0.imprint","IMPRINT",EDGE,{"derivedFrom":sQuery(id+"F0.wireOp",EDGE,"E5.2.0.1")}),1.0]])]});
            var Q15;
            Q15=makeQuery(id+"F0.imprint","IMPRINT",FACE,{"disambiguationData":[TD([[makeQuery(id+"F0.imprint","IMPRINT",EDGE,{"derivedFrom":sQuery(id+"F0.wireOp",EDGE,"E5.3.1.1")}),1.0]])]});
            var Q16;
            Q16=makeQuery(id+"F0.imprint","IMPRINT",FACE,{"disambiguationData":[TD([[makeQuery(id+"F0.imprint","IMPRINT",EDGE,{"derivedFrom":sQuery(id+"F0.wireOp",EDGE,"E5.3.2.1")}),1.0]])]});
            var Q17;
            Q17=makeQuery(id+"F0.imprint","IMPRINT",FACE,{"disambiguationData":[TD([[makeQuery(id+"F0.imprint","IMPRINT",EDGE,{"derivedFrom":sQuery(id+"F0.wireOp",EDGE,"E5.3.3.1")}),1.0]])]});
            var Q18;
            Q18=makeQuery(id+"F0.imprint","IMPRINT",FACE,{"disambiguationData":[TD([[makeQuery(id+"F0.imprint","IMPRINT",EDGE,{"derivedFrom":sQuery(id+"F0.wireOp",EDGE,"E5.3.4.1")}),1.0]])]});
            var Q19;
            Q19=makeQuery(id+"F0.imprint","IMPRINT",FACE,{"disambiguationData":[TD([[makeQuery(id+"F0.imprint","IMPRINT",EDGE,{"derivedFrom":sQuery(id+"F0.wireOp",EDGE,"E0.bottom")}),1.0]])]});
            var Q20;
            Q20=makeQuery(id+"F0.imprint","IMPRINT",FACE,{"disambiguationData":[TD([[makeQuery(id+"F0.imprint","IMPRINT",EDGE,{"derivedFrom":sQuery(id+"F0.wireOp",EDGE,"E0.bottom")}),-1.0]])]});
            extrude(context, id + "F2", {"entities" : qUnion([Q0, Q1, Q2, Q3, Q4, Q5, Q6, Q7, Q8, Q9, Q10, Q11, Q12, Q13, Q14, Q15, Q16, Q17, Q18, Q19, Q20]), "operationType" : NewBodyOperationType.ADD, "oppositeDirection" : true, "depth" : 3 * mm});
        }
    });
